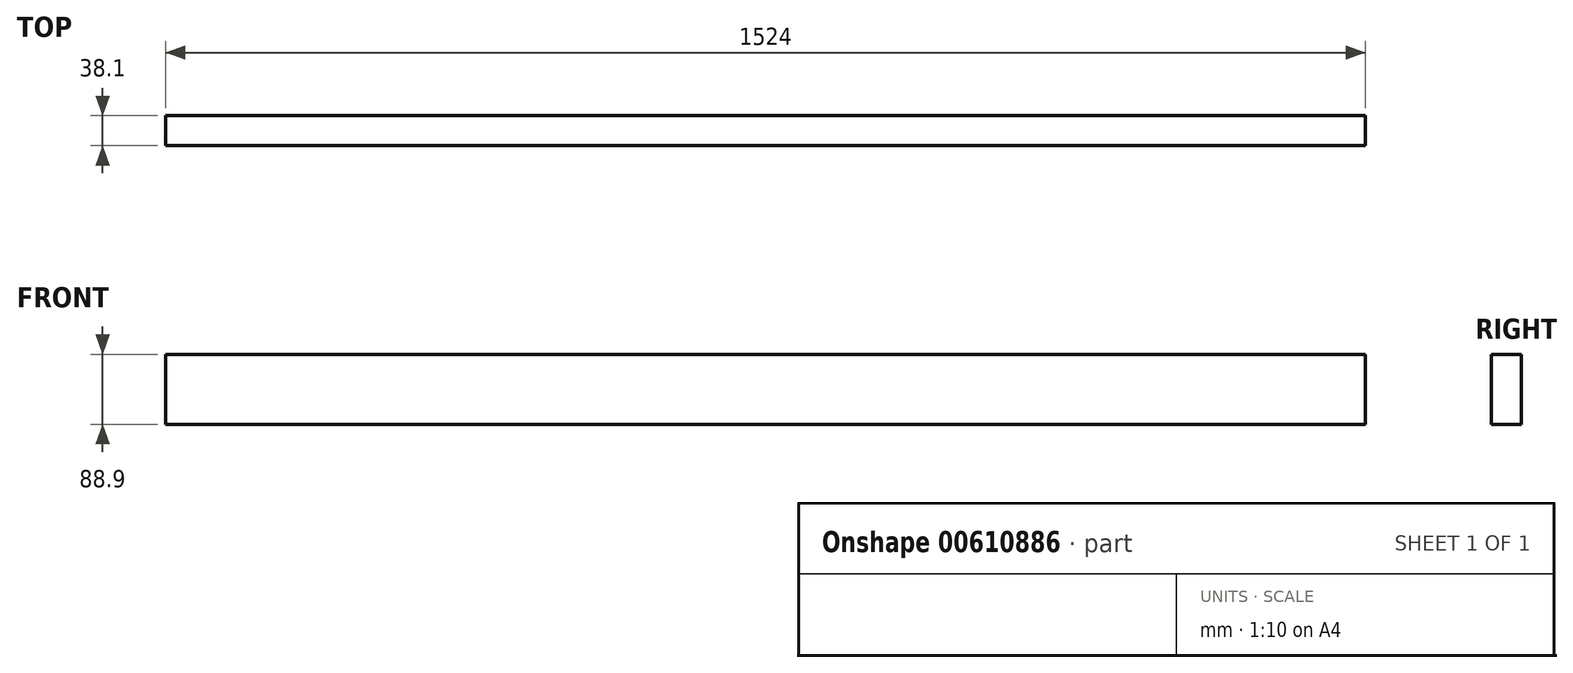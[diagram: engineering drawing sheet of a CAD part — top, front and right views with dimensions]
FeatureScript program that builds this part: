
annotation { "Feature Type Name" : "Feature", "Feature Type Description" : "" }
export const myFeature = defineFeature(function(context is Context, id is Id, definition is map)
    precondition{}
    {
        {
            var Q0;
            Q0=qCreatedBy(makeId("Front.planeOp"),FACE);
            var sketch = newSketch(context, id + "F0", { "sketchPlane" : qUnion([Q0])});
            skLineSegment(sketch, "E0.bottom", {"start": v(762, -44.45) * mm, "end": v(-762, -44.45) * mm});
            skLineSegment(sketch, "E0.top", {"start": v(762, 44.45) * mm, "end": v(-762, 44.45) * mm});
            skLineSegment(sketch, "E0.left", {"start": v(762, -44.45) * mm, "end": v(762, 44.45) * mm});
            skLineSegment(sketch, "E0.right", {"start": v(-762, -44.45) * mm, "end": v(-762, 44.45) * mm});
            skPoint(sketch, "E0.middle", {"position": v(0, 0) * mm});
            skSolve(sketch);
        }
        {
            var Q0;
            Q0=makeQuery(id+"F0.imprint","IMPRINT",FACE,{"disambiguationData":[TD([[makeQuery(id+"F0.imprint","IMPRINT",EDGE,{"derivedFrom":sQuery(id+"F0.wireOp",EDGE,"E0.bottom")}),-1.0]])]});
            extrude(context, id + "F1", {"entities" : qUnion([Q0]), "depth" : 38.1 * mm, "offsetDistance" : 25.4 * mm});
        }
    });
